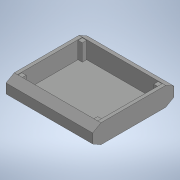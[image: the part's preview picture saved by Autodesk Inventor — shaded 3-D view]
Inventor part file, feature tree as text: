
AUTODESK INVENTOR PART (.ipt)
format: ipt  version: 2020 (Build 240168000, 168)  size: 157,184 bytes
history: native  units: in
note: dims shown in document units (in); Inventor stores cm internally (conversion verified against a paired STEP export)
features: extrude x3, sketch x3, projected_geometry x3
ambient origin geometry x8: Origin, YZ Plane, XZ Plane, XY Plane, X Axis, Y Axis, Z Axis, Center Point
bodies: Solid1 (feature_tree)
feature tree (9):
  extrude  "Extrusion1"  Depth=5.9055in
  extrude  "Extrusion2"  TaperAngle=0.0deg  [1 undecoded]
  extrude  "Extrusion3"  Depth=1.2598in
  sketch  "Sketch1"  dims[d0=1.378in d1=5.9055in]
  sketch  "Sketch2"  dims[d2=6.2992in d3=0.0in]
  projected_geometry  "Projected Loop1"
  sketch  "Sketch3"  dims[d4=0.2362in d5=1.2598in d6=0.0in d8=0.315in d10=1.2205in d11=0.0in]
  projected_geometry  "Projected Loop2"
  projected_geometry  "Projected Loop3"
note: 1 required parameter value undecoded (feature->parameter linkage not recoverable at this tier; creation-order binding heuristic only, values carry confidence <= 0.55)
